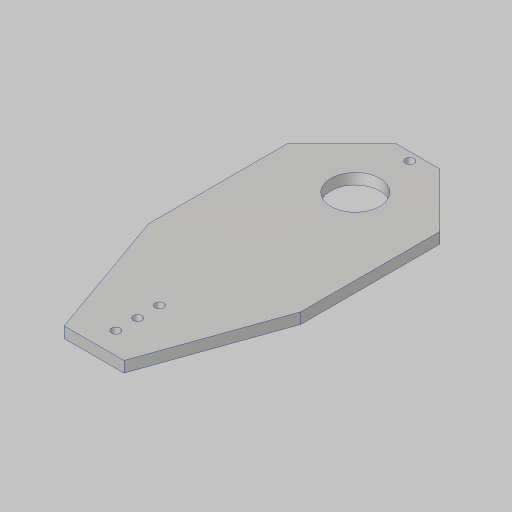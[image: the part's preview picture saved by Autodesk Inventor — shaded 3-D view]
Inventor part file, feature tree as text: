
AUTODESK INVENTOR PART (.ipt)
format: ipt  version: 2023.5 (Build 275446000, 446)  size: 207,360 bytes
history: native  units: in
note: dims shown in document units (in); Inventor stores cm internally (conversion verified against a paired STEP export)
features: sketch x3, extrude x2, hole x2, projected_geometry x1
ambient origin geometry x8: Origin, YZ Plane, XZ Plane, XY Plane, X Axis, Y Axis, Z Axis, Center Point
bodies: Solid1 (feature_tree)
feature tree (8):
  sketch  "Sketch1"  dims[d0=2.0in d1=1.0in]
  extrude  "Extrusion1"  Depth=1.0in
  hole  "Hole1"  [1 undecoded]
  extrude  "Extrusion2"  Depth=0.25in
  hole  "Hole2"  [1 undecoded]
  sketch  "Sketch2"  dims[d2=3.5in d4=1.125in]
  sketch  "Sketch3"  dims[d5=0.375in d6=1.25in d7=6.0in d8=0.25in d9=0.0in d11=0.201in d12=0.75in d13=0.385in d14=0.25in d15=0.5635in d16=1.0in d17=0.8108in d18=1.0in d19=1.25in d20=1.25in d21=1.0in d22=2.0in d23=1.375in d24=3.0in d25=0.0in d26=0.0in d27=0.5in d28=1.0in d29=0.201in d30=0.38in d31=0.385in d32=0.25in d33=0.5635in d34=1.0in d35=0.8108in]
  projected_geometry  "Project Cut Edges1"
note: 2 required parameter values undecoded (feature->parameter linkage not recoverable at this tier; creation-order binding heuristic only, values carry confidence <= 0.55)
